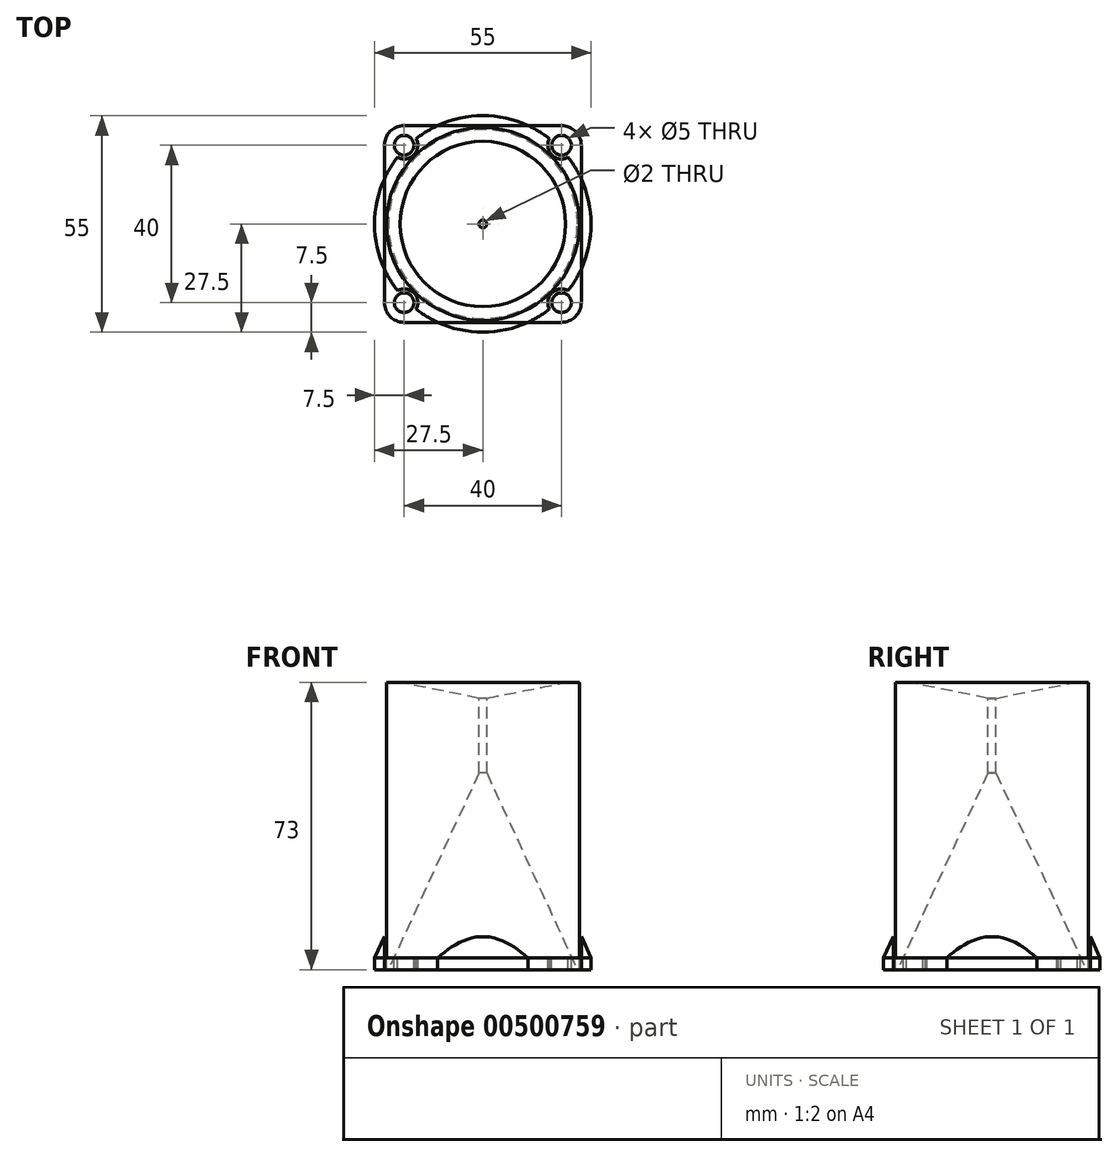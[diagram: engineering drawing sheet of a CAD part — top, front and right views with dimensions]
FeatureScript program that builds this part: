
annotation { "Feature Type Name" : "Feature", "Feature Type Description" : "" }
export const myFeature = defineFeature(function(context is Context, id is Id, definition is map)
    precondition{}
    {
        {
            var Q0;
            Q0=qCreatedBy(makeId("Top.planeOp"),FACE);
            var sketch = newSketch(context, id + "F0", { "sketchPlane" : qUnion([Q0])});
            skLineSegment(sketch, "E0.bottom", {"start": v(-25, 25) * mm, "end": v(25, 25) * mm});
            skLineSegment(sketch, "E0.top", {"start": v(-25, -25) * mm, "end": v(25, -25) * mm});
            skLineSegment(sketch, "E0.left", {"start": v(-25, 25) * mm, "end": v(-25, -25) * mm});
            skLineSegment(sketch, "E0.right", {"start": v(25, 25) * mm, "end": v(25, -25) * mm});
            skCircle(sketch, "E1", {"center": v(20, 20) * mm, "radius": 2.5 * mm});
            skCircle(sketch, "E2", {"center": v(20, -20) * mm, "radius": 2.5 * mm});
            skCircle(sketch, "E3", {"center": v(-20, -20) * mm, "radius": 2.5 * mm});
            skCircle(sketch, "E4", {"center": v(-20, 20) * mm, "radius": 2.5 * mm});
            skCircle(sketch, "E5", {"center": v(0, 0) * mm, "radius": 24.5 * mm});
            skCircle(sketch, "E6", {"center": v(-20, 20) * mm, "radius": 3.5 * mm});
            skCircle(sketch, "E7", {"center": v(20, 20) * mm, "radius": 3.5 * mm});
            skCircle(sketch, "E8", {"center": v(20, -20) * mm, "radius": 3.5 * mm});
            skCircle(sketch, "E9", {"center": v(-20, -20) * mm, "radius": 3.5 * mm});
            skCircle(sketch, "E10", {"center": v(0, 0) * mm, "radius": 1 * mm});
            skCircle(sketch, "E11", {"center": v(0, 0) * mm, "radius": 27.5 * mm});
            skSolve(sketch);
        }
        {
            var Q0;
            Q0=makeQuery(id+"F0.imprint","IMPRINT",FACE,{"disambiguationData":[TD([[makeQuery(id+"F0.imprint","IMPRINT",EDGE,{"derivedFrom":sQuery(id+"F0.wireOp",EDGE,"E0.bottom")}),-1.0]])]});
            var Q1;
            Q1=makeQuery(id+"F0.imprint","IMPRINT",FACE,{"disambiguationData":[TD([[makeQuery(id+"F0.imprint","IMPRINT",EDGE,{"derivedFrom":sQuery(id+"F0.wireOp",EDGE,"E1")}),-1.0]])]});
            var Q2;
            Q2=makeQuery(id+"F0.imprint","IMPRINT",FACE,{"disambiguationData":[TD([[makeQuery(id+"F0.imprint","IMPRINT",EDGE,{"derivedFrom":sQuery(id+"F0.wireOp",EDGE,"E2")}),-1.0]])]});
            var Q3;
            Q3=makeQuery(id+"F0.imprint","IMPRINT",FACE,{"disambiguationData":[TD([[makeQuery(id+"F0.imprint","IMPRINT",EDGE,{"derivedFrom":sQuery(id+"F0.wireOp",EDGE,"E3")}),-1.0]])]});
            var Q4;
            Q4=makeQuery(id+"F0.imprint","IMPRINT",FACE,{"disambiguationData":[TD([[makeQuery(id+"F0.imprint","IMPRINT",EDGE,{"derivedFrom":sQuery(id+"F0.wireOp",EDGE,"E4")}),-1.0]])]});
            var Q5;
            Q5=makeQuery(id+"F0.imprint","IMPRINT",FACE,{"disambiguationData":[TD([[makeQuery(id+"F0.imprint","IMPRINT",EDGE,{"derivedFrom":sQuery(id+"F0.wireOp",EDGE,"E5")}),1.0]])]});
            var Q6;
            Q6=makeQuery(id+"F0.imprint","IMPRINT",FACE,{"disambiguationData":[TD([[makeQuery(id+"F0.imprint","IMPRINT",EDGE,{"derivedFrom":sQuery(id+"F0.wireOp",EDGE,"WA1lCMuK-sLq4-XsFw-FNTR-WKbZTbo29WLb")}),1.0]])]});
            var Q7;
            Q7=makeQuery(id+"F0.imprint","IMPRINT",FACE,{"disambiguationData":[TD([[makeQuery(id+"F0.imprint","IMPRINT",EDGE,{"derivedFrom":sQuery(id+"F0.wireOp",EDGE,"E5")}),-1.0]])]});
            var Q8;
            {var subQ0=sQuery(id+"F0.wireOp",EDGE,"E11");var subQ1=sQuery(id+"F0.wireOp",EDGE,"E0.bottom");var subQ2=makeQuery(id+"F0.imprint","INTERSECT",VERTEX,{"disambiguationData":[OD(0.0)],"derivedFrom":[subQ1,subQ0]});Q8=makeQuery(id+"F0.imprint","IMPRINT",FACE,{"disambiguationData":[TD([[makeQuery(id+"F0.imprint","IMPRINT",EDGE,{"disambiguationData":[TD([[subQ2,-1.0]])],"derivedFrom":subQ1}),1.0]])]});}
            var Q9;
            {var subQ0=sQuery(id+"F0.wireOp",EDGE,"E11");var subQ1=sQuery(id+"F0.wireOp",EDGE,"E0.right");var subQ2=makeQuery(id+"F0.imprint","INTERSECT",VERTEX,{"disambiguationData":[OD(0.0)],"derivedFrom":[subQ1,subQ0]});Q9=makeQuery(id+"F0.imprint","IMPRINT",FACE,{"disambiguationData":[TD([[makeQuery(id+"F0.imprint","IMPRINT",EDGE,{"disambiguationData":[TD([[subQ2,-1.0]])],"derivedFrom":subQ1}),1.0]])]});}
            var Q10;
            {var subQ0=sQuery(id+"F0.wireOp",EDGE,"E11");var subQ1=sQuery(id+"F0.wireOp",EDGE,"E0.left");var subQ2=makeQuery(id+"F0.imprint","INTERSECT",VERTEX,{"disambiguationData":[OD(0.0)],"derivedFrom":[subQ1,subQ0]});Q10=makeQuery(id+"F0.imprint","IMPRINT",FACE,{"disambiguationData":[TD([[makeQuery(id+"F0.imprint","IMPRINT",EDGE,{"disambiguationData":[TD([[subQ2,-1.0]])],"derivedFrom":subQ1}),-1.0]])]});}
            var Q11;
            {var subQ0=sQuery(id+"F0.wireOp",EDGE,"E11");var subQ1=sQuery(id+"F0.wireOp",EDGE,"E0.top");var subQ2=makeQuery(id+"F0.imprint","INTERSECT",VERTEX,{"disambiguationData":[OD(0.0)],"derivedFrom":[subQ1,subQ0]});Q11=makeQuery(id+"F0.imprint","IMPRINT",FACE,{"disambiguationData":[TD([[makeQuery(id+"F0.imprint","IMPRINT",EDGE,{"disambiguationData":[TD([[subQ2,-1.0]])],"derivedFrom":subQ1}),-1.0]])]});}
            var Q12;
            {var subQ1=sQuery(id+"F0.wireOp",EDGE,"E0.top");var subQ6=sQuery(id+"F0.wireOp",EDGE,"E0.right");var subQ7=makeQuery(id+"F0.imprint","INTERSECT",VERTEX,{"derivedFrom":[subQ1,subQ6]});Q12=makeQuery(id+"F0.imprint","IMPRINT",FACE,{"disambiguationData":[TD([[makeQuery(id+"F0.imprint","IMPRINT",EDGE,{"disambiguationData":[TD([[subQ7,1.0]])],"derivedFrom":subQ1}),1.0]])]});}
            var Q13;
            {var subQ1=sQuery(id+"F0.wireOp",EDGE,"E0.left");var subQ6=sQuery(id+"F0.wireOp",EDGE,"E0.top");var subQ7=makeQuery(id+"F0.imprint","INTERSECT",VERTEX,{"derivedFrom":[subQ6,subQ1]});Q13=makeQuery(id+"F0.imprint","IMPRINT",FACE,{"disambiguationData":[TD([[makeQuery(id+"F0.imprint","IMPRINT",EDGE,{"disambiguationData":[TD([[subQ7,-1.0]])],"derivedFrom":subQ6}),1.0]])]});}
            extrude(context, id + "F1", {"entities" : qUnion([Q0, Q1, Q2, Q3, Q4, Q5, Q6, Q7, Q8, Q9, Q10, Q11, Q12, Q13]), "oppositeDirection" : true, "depth" : 3 * mm, "offsetDistance" : 25 * mm});
        }
        {
            var Q0;
            Q0=makeQuery(id+"F1.opExtrude","SWEPT_EDGE",EDGE,{"disambiguationData":[OSD([sQuery(id+"F0.wireOp",EDGE,"E0.bottom"),sQuery(id+"F0.wireOp",EDGE,"E0.left")])]});
            var Q1;
            Q1=makeQuery(id+"F1.opExtrude","SWEPT_EDGE",EDGE,{"disambiguationData":[OSD([sQuery(id+"F0.wireOp",EDGE,"E0.top"),sQuery(id+"F0.wireOp",EDGE,"E0.left")])]});
            var Q2;
            Q2=makeQuery(id+"F1.opExtrude","SWEPT_EDGE",EDGE,{"disambiguationData":[OSD([sQuery(id+"F0.wireOp",EDGE,"E0.top"),sQuery(id+"F0.wireOp",EDGE,"E0.right")])]});
            var Q3;
            Q3=makeQuery(id+"F1.opExtrude","SWEPT_EDGE",EDGE,{"disambiguationData":[OSD([sQuery(id+"F0.wireOp",EDGE,"E0.bottom"),sQuery(id+"F0.wireOp",EDGE,"E0.right")])]});
            fillet(context, id + "F2", {"entities" : qUnion([Q0, Q1, Q2, Q3]), "radius" : 5 * mm, "tangentPropagation" : true, "allowEdgeOverflow" : false});
        }
        {
            var Q0;
            Q0=makeQuery(id+"F0.imprint","IMPRINT",FACE,{"disambiguationData":[TD([[makeQuery(id+"F0.imprint","IMPRINT",EDGE,{"derivedFrom":sQuery(id+"F0.wireOp",EDGE,"E5")}),1.0]])]});
            var Q1;
            Q1=makeQuery(id+"F0.imprint","IMPRINT",FACE,{"disambiguationData":[TD([[makeQuery(id+"F0.imprint","IMPRINT",EDGE,{"derivedFrom":sQuery(id+"F0.wireOp",EDGE,"E5")}),-1.0]])]});
            var Q2;
            {var subQ0=sQuery(id+"F0.wireOp",EDGE,"E11");var subQ1=sQuery(id+"F0.wireOp",EDGE,"E1");var subQ2=makeQuery(id+"F0.imprint","INTERSECT",VERTEX,{"disambiguationData":[OD(0.0)],"derivedFrom":[subQ1,subQ0]});Q2=makeQuery(id+"F0.imprint","IMPRINT",FACE,{"disambiguationData":[TD([[makeQuery(id+"F0.imprint","IMPRINT",EDGE,{"disambiguationData":[TD([[subQ2,1.0]])],"derivedFrom":subQ1}),1.0]])]});}
            var Q3;
            {var subQ0=sQuery(id+"F0.wireOp",EDGE,"E11");var subQ1=sQuery(id+"F0.wireOp",EDGE,"E4");var subQ2=makeQuery(id+"F0.imprint","INTERSECT",VERTEX,{"disambiguationData":[OD(0.0)],"derivedFrom":[subQ1,subQ0]});Q3=makeQuery(id+"F0.imprint","IMPRINT",FACE,{"disambiguationData":[TD([[makeQuery(id+"F0.imprint","IMPRINT",EDGE,{"disambiguationData":[TD([[subQ2,1.0]])],"derivedFrom":subQ1}),-1.0]])]});}
            var Q4;
            {var subQ0=sQuery(id+"F0.wireOp",EDGE,"E11");var subQ1=sQuery(id+"F0.wireOp",EDGE,"E4");var subQ2=makeQuery(id+"F0.imprint","INTERSECT",VERTEX,{"disambiguationData":[OD(0.0)],"derivedFrom":[subQ1,subQ0]});Q4=makeQuery(id+"F0.imprint","IMPRINT",FACE,{"disambiguationData":[TD([[makeQuery(id+"F0.imprint","IMPRINT",EDGE,{"disambiguationData":[TD([[subQ2,1.0]])],"derivedFrom":subQ1}),1.0]])]});}
            var Q5;
            {var subQ0=sQuery(id+"F0.wireOp",EDGE,"E11");var subQ1=sQuery(id+"F0.wireOp",EDGE,"E0.left");var subQ2=makeQuery(id+"F0.imprint","INTERSECT",VERTEX,{"disambiguationData":[OD(0.0)],"derivedFrom":[subQ1,subQ0]});Q5=makeQuery(id+"F0.imprint","IMPRINT",FACE,{"disambiguationData":[TD([[makeQuery(id+"F0.imprint","IMPRINT",EDGE,{"disambiguationData":[TD([[subQ2,-1.0]])],"derivedFrom":subQ1}),-1.0]])]});}
            var Q6;
            {var subQ0=sQuery(id+"F0.wireOp",EDGE,"E11");var subQ1=sQuery(id+"F0.wireOp",EDGE,"E0.bottom");var subQ2=makeQuery(id+"F0.imprint","INTERSECT",VERTEX,{"disambiguationData":[OD(0.0)],"derivedFrom":[subQ1,subQ0]});Q6=makeQuery(id+"F0.imprint","IMPRINT",FACE,{"disambiguationData":[TD([[makeQuery(id+"F0.imprint","IMPRINT",EDGE,{"disambiguationData":[TD([[subQ2,-1.0]])],"derivedFrom":subQ1}),1.0]])]});}
            var Q7;
            {var subQ0=sQuery(id+"F0.wireOp",EDGE,"E11");var subQ1=sQuery(id+"F0.wireOp",EDGE,"E1");var subQ2=makeQuery(id+"F0.imprint","INTERSECT",VERTEX,{"disambiguationData":[OD(0.0)],"derivedFrom":[subQ1,subQ0]});Q7=makeQuery(id+"F0.imprint","IMPRINT",FACE,{"disambiguationData":[TD([[makeQuery(id+"F0.imprint","IMPRINT",EDGE,{"disambiguationData":[TD([[subQ2,1.0]])],"derivedFrom":subQ1}),-1.0]])]});}
            var Q8;
            {var subQ0=sQuery(id+"F0.wireOp",EDGE,"E11");var subQ1=sQuery(id+"F0.wireOp",EDGE,"E0.right");var subQ2=makeQuery(id+"F0.imprint","INTERSECT",VERTEX,{"disambiguationData":[OD(0.0)],"derivedFrom":[subQ1,subQ0]});Q8=makeQuery(id+"F0.imprint","IMPRINT",FACE,{"disambiguationData":[TD([[makeQuery(id+"F0.imprint","IMPRINT",EDGE,{"disambiguationData":[TD([[subQ2,-1.0]])],"derivedFrom":subQ1}),1.0]])]});}
            var Q9;
            {var subQ0=sQuery(id+"F0.wireOp",EDGE,"E11");var subQ1=sQuery(id+"F0.wireOp",EDGE,"E2");var subQ2=makeQuery(id+"F0.imprint","INTERSECT",VERTEX,{"disambiguationData":[OD(0.0)],"derivedFrom":[subQ1,subQ0]});Q9=makeQuery(id+"F0.imprint","IMPRINT",FACE,{"disambiguationData":[TD([[makeQuery(id+"F0.imprint","IMPRINT",EDGE,{"disambiguationData":[TD([[subQ2,1.0]])],"derivedFrom":subQ1}),-1.0]])]});}
            var Q10;
            {var subQ0=sQuery(id+"F0.wireOp",EDGE,"E11");var subQ1=sQuery(id+"F0.wireOp",EDGE,"E2");var subQ2=makeQuery(id+"F0.imprint","INTERSECT",VERTEX,{"disambiguationData":[OD(0.0)],"derivedFrom":[subQ1,subQ0]});Q10=makeQuery(id+"F0.imprint","IMPRINT",FACE,{"disambiguationData":[TD([[makeQuery(id+"F0.imprint","IMPRINT",EDGE,{"disambiguationData":[TD([[subQ2,1.0]])],"derivedFrom":subQ1}),1.0]])]});}
            var Q11;
            {var subQ0=sQuery(id+"F0.wireOp",EDGE,"E11");var subQ1=sQuery(id+"F0.wireOp",EDGE,"E0.top");var subQ2=makeQuery(id+"F0.imprint","INTERSECT",VERTEX,{"disambiguationData":[OD(0.0)],"derivedFrom":[subQ1,subQ0]});Q11=makeQuery(id+"F0.imprint","IMPRINT",FACE,{"disambiguationData":[TD([[makeQuery(id+"F0.imprint","IMPRINT",EDGE,{"disambiguationData":[TD([[subQ2,-1.0]])],"derivedFrom":subQ1}),-1.0]])]});}
            var Q12;
            {var subQ0=sQuery(id+"F0.wireOp",EDGE,"E11");var subQ1=sQuery(id+"F0.wireOp",EDGE,"E3");var subQ2=makeQuery(id+"F0.imprint","INTERSECT",VERTEX,{"disambiguationData":[OD(0.0)],"derivedFrom":[subQ1,subQ0]});Q12=makeQuery(id+"F0.imprint","IMPRINT",FACE,{"disambiguationData":[TD([[makeQuery(id+"F0.imprint","IMPRINT",EDGE,{"disambiguationData":[TD([[subQ2,1.0]])],"derivedFrom":subQ1}),1.0]])]});}
            var Q13;
            {var subQ0=sQuery(id+"F0.wireOp",EDGE,"E11");var subQ1=sQuery(id+"F0.wireOp",EDGE,"E3");var subQ2=makeQuery(id+"F0.imprint","INTERSECT",VERTEX,{"disambiguationData":[OD(0.0)],"derivedFrom":[subQ1,subQ0]});Q13=makeQuery(id+"F0.imprint","IMPRINT",FACE,{"disambiguationData":[TD([[makeQuery(id+"F0.imprint","IMPRINT",EDGE,{"disambiguationData":[TD([[subQ2,1.0]])],"derivedFrom":subQ1}),-1.0]])]});}
            extrude(context, id + "F3", {"entities" : qUnion([Q0, Q1, Q2, Q3, Q4, Q5, Q6, Q7, Q8, Q9, Q10, Q11, Q12, Q13]), "operationType" : NewBodyOperationType.ADD, "depth" : 50 * mm, "offsetDistance" : 25 * mm});
        }
        {
            var Q0;
            Q0=makeQuery(id+"F3.opExtrude","CAP_EDGE",EDGE,{"disambiguationData":[OSD([sQuery(id+"F0.wireOp",EDGE,"E11")])],"isStart":false});
            chamfer(context, id + "F4", {"entities" : qUnion([Q0]), "chamferType" : ChamferType.TWO_OFFSETS, "width1" : 23 * mm, "oppositeDirection" : false, "width2" : 50 * mm, "tangentPropagation" : true});
        }
        {
            var Q0;
            {var subQ0=sQuery(id+"F0.wireOp",EDGE,"E11");var subQ1=sQuery(id+"F0.wireOp",EDGE,"E1");var subQ2=makeQuery(id+"F0.imprint","INTERSECT",VERTEX,{"disambiguationData":[OD(0.0)],"derivedFrom":[subQ1,subQ0]});Q0=makeQuery(id+"F0.imprint","IMPRINT",FACE,{"disambiguationData":[TD([[makeQuery(id+"F0.imprint","IMPRINT",EDGE,{"disambiguationData":[TD([[subQ2,1.0]])],"derivedFrom":subQ1}),1.0]])]});}
            var Q1;
            {var subQ0=sQuery(id+"F0.wireOp",EDGE,"E11");var subQ1=sQuery(id+"F0.wireOp",EDGE,"E1");var subQ2=makeQuery(id+"F0.imprint","INTERSECT",VERTEX,{"disambiguationData":[OD(0.0)],"derivedFrom":[subQ1,subQ0]});Q1=makeQuery(id+"F0.imprint","IMPRINT",FACE,{"disambiguationData":[TD([[makeQuery(id+"F0.imprint","IMPRINT",EDGE,{"disambiguationData":[TD([[subQ2,1.0]])],"derivedFrom":subQ1}),-1.0]])]});}
            var Q2;
            {var subQ0=sQuery(id+"F0.wireOp",EDGE,"E11");var subQ1=sQuery(id+"F0.wireOp",EDGE,"E1");var subQ2=makeQuery(id+"F0.imprint","INTERSECT",VERTEX,{"disambiguationData":[OD(0.0)],"derivedFrom":[subQ1,subQ0]});Q2=makeQuery(id+"F0.imprint","IMPRINT",FACE,{"disambiguationData":[TD([[makeQuery(id+"F0.imprint","IMPRINT",EDGE,{"disambiguationData":[TD([[subQ2,-1.0]])],"derivedFrom":subQ1}),-1.0]])]});}
            var Q3;
            {var subQ0=sQuery(id+"F0.wireOp",EDGE,"E11");var subQ1=sQuery(id+"F0.wireOp",EDGE,"E4");var subQ2=makeQuery(id+"F0.imprint","INTERSECT",VERTEX,{"disambiguationData":[OD(0.0)],"derivedFrom":[subQ1,subQ0]});Q3=makeQuery(id+"F0.imprint","IMPRINT",FACE,{"disambiguationData":[TD([[makeQuery(id+"F0.imprint","IMPRINT",EDGE,{"disambiguationData":[TD([[subQ2,1.0]])],"derivedFrom":subQ1}),1.0]])]});}
            var Q4;
            {var subQ0=sQuery(id+"F0.wireOp",EDGE,"E11");var subQ1=sQuery(id+"F0.wireOp",EDGE,"E4");var subQ2=makeQuery(id+"F0.imprint","INTERSECT",VERTEX,{"disambiguationData":[OD(0.0)],"derivedFrom":[subQ1,subQ0]});Q4=makeQuery(id+"F0.imprint","IMPRINT",FACE,{"disambiguationData":[TD([[makeQuery(id+"F0.imprint","IMPRINT",EDGE,{"disambiguationData":[TD([[subQ2,1.0]])],"derivedFrom":subQ1}),-1.0]])]});}
            var Q5;
            {var subQ0=sQuery(id+"F0.wireOp",EDGE,"E11");var subQ1=sQuery(id+"F0.wireOp",EDGE,"E4");var subQ2=makeQuery(id+"F0.imprint","INTERSECT",VERTEX,{"disambiguationData":[OD(0.0)],"derivedFrom":[subQ1,subQ0]});Q5=makeQuery(id+"F0.imprint","IMPRINT",FACE,{"disambiguationData":[TD([[makeQuery(id+"F0.imprint","IMPRINT",EDGE,{"disambiguationData":[TD([[subQ2,-1.0]])],"derivedFrom":subQ1}),-1.0]])]});}
            var Q6;
            {var subQ0=sQuery(id+"F0.wireOp",EDGE,"E11");var subQ1=sQuery(id+"F0.wireOp",EDGE,"E4");var subQ2=makeQuery(id+"F0.imprint","INTERSECT",VERTEX,{"disambiguationData":[OD(0.0)],"derivedFrom":[subQ1,subQ0]});Q6=makeQuery(id+"F0.imprint","IMPRINT",FACE,{"disambiguationData":[TD([[makeQuery(id+"F0.imprint","IMPRINT",EDGE,{"disambiguationData":[TD([[subQ2,-1.0]])],"derivedFrom":subQ1}),1.0]])]});}
            var Q7;
            {var subQ0=sQuery(id+"F0.wireOp",EDGE,"E11");var subQ1=sQuery(id+"F0.wireOp",EDGE,"E1");var subQ2=makeQuery(id+"F0.imprint","INTERSECT",VERTEX,{"disambiguationData":[OD(0.0)],"derivedFrom":[subQ1,subQ0]});Q7=makeQuery(id+"F0.imprint","IMPRINT",FACE,{"disambiguationData":[TD([[makeQuery(id+"F0.imprint","IMPRINT",EDGE,{"disambiguationData":[TD([[subQ2,-1.0]])],"derivedFrom":subQ1}),1.0]])]});}
            var Q8;
            {var subQ0=sQuery(id+"F0.wireOp",EDGE,"E11");var subQ1=sQuery(id+"F0.wireOp",EDGE,"E2");var subQ2=makeQuery(id+"F0.imprint","INTERSECT",VERTEX,{"disambiguationData":[OD(0.0)],"derivedFrom":[subQ1,subQ0]});Q8=makeQuery(id+"F0.imprint","IMPRINT",FACE,{"disambiguationData":[TD([[makeQuery(id+"F0.imprint","IMPRINT",EDGE,{"disambiguationData":[TD([[subQ2,1.0]])],"derivedFrom":subQ1}),1.0]])]});}
            var Q9;
            {var subQ0=sQuery(id+"F0.wireOp",EDGE,"E11");var subQ1=sQuery(id+"F0.wireOp",EDGE,"E2");var subQ2=makeQuery(id+"F0.imprint","INTERSECT",VERTEX,{"disambiguationData":[OD(0.0)],"derivedFrom":[subQ1,subQ0]});Q9=makeQuery(id+"F0.imprint","IMPRINT",FACE,{"disambiguationData":[TD([[makeQuery(id+"F0.imprint","IMPRINT",EDGE,{"disambiguationData":[TD([[subQ2,-1.0]])],"derivedFrom":subQ1}),1.0]])]});}
            var Q10;
            {var subQ0=sQuery(id+"F0.wireOp",EDGE,"E11");var subQ1=sQuery(id+"F0.wireOp",EDGE,"E2");var subQ2=makeQuery(id+"F0.imprint","INTERSECT",VERTEX,{"disambiguationData":[OD(0.0)],"derivedFrom":[subQ1,subQ0]});Q10=makeQuery(id+"F0.imprint","IMPRINT",FACE,{"disambiguationData":[TD([[makeQuery(id+"F0.imprint","IMPRINT",EDGE,{"disambiguationData":[TD([[subQ2,-1.0]])],"derivedFrom":subQ1}),-1.0]])]});}
            var Q11;
            {var subQ0=sQuery(id+"F0.wireOp",EDGE,"E11");var subQ1=sQuery(id+"F0.wireOp",EDGE,"E2");var subQ2=makeQuery(id+"F0.imprint","INTERSECT",VERTEX,{"disambiguationData":[OD(0.0)],"derivedFrom":[subQ1,subQ0]});Q11=makeQuery(id+"F0.imprint","IMPRINT",FACE,{"disambiguationData":[TD([[makeQuery(id+"F0.imprint","IMPRINT",EDGE,{"disambiguationData":[TD([[subQ2,1.0]])],"derivedFrom":subQ1}),-1.0]])]});}
            var Q12;
            {var subQ0=sQuery(id+"F0.wireOp",EDGE,"E11");var subQ1=sQuery(id+"F0.wireOp",EDGE,"E3");var subQ2=makeQuery(id+"F0.imprint","INTERSECT",VERTEX,{"disambiguationData":[OD(0.0)],"derivedFrom":[subQ1,subQ0]});Q12=makeQuery(id+"F0.imprint","IMPRINT",FACE,{"disambiguationData":[TD([[makeQuery(id+"F0.imprint","IMPRINT",EDGE,{"disambiguationData":[TD([[subQ2,-1.0]])],"derivedFrom":subQ1}),1.0]])]});}
            var Q13;
            {var subQ0=sQuery(id+"F0.wireOp",EDGE,"E11");var subQ1=sQuery(id+"F0.wireOp",EDGE,"E3");var subQ2=makeQuery(id+"F0.imprint","INTERSECT",VERTEX,{"disambiguationData":[OD(0.0)],"derivedFrom":[subQ1,subQ0]});Q13=makeQuery(id+"F0.imprint","IMPRINT",FACE,{"disambiguationData":[TD([[makeQuery(id+"F0.imprint","IMPRINT",EDGE,{"disambiguationData":[TD([[subQ2,1.0]])],"derivedFrom":subQ1}),1.0]])]});}
            var Q14;
            {var subQ0=sQuery(id+"F0.wireOp",EDGE,"E11");var subQ1=sQuery(id+"F0.wireOp",EDGE,"E3");var subQ2=makeQuery(id+"F0.imprint","INTERSECT",VERTEX,{"disambiguationData":[OD(0.0)],"derivedFrom":[subQ1,subQ0]});Q14=makeQuery(id+"F0.imprint","IMPRINT",FACE,{"disambiguationData":[TD([[makeQuery(id+"F0.imprint","IMPRINT",EDGE,{"disambiguationData":[TD([[subQ2,1.0]])],"derivedFrom":subQ1}),-1.0]])]});}
            var Q15;
            {var subQ0=sQuery(id+"F0.wireOp",EDGE,"E11");var subQ1=sQuery(id+"F0.wireOp",EDGE,"E3");var subQ2=makeQuery(id+"F0.imprint","INTERSECT",VERTEX,{"disambiguationData":[OD(0.0)],"derivedFrom":[subQ1,subQ0]});Q15=makeQuery(id+"F0.imprint","IMPRINT",FACE,{"disambiguationData":[TD([[makeQuery(id+"F0.imprint","IMPRINT",EDGE,{"disambiguationData":[TD([[subQ2,-1.0]])],"derivedFrom":subQ1}),-1.0]])]});}
            extrude(context, id + "F5", {"entities" : qUnion([Q0, Q1, Q2, Q3, Q4, Q5, Q6, Q7, Q8, Q9, Q10, Q11, Q12, Q13, Q14, Q15]), "operationType" : NewBodyOperationType.REMOVE, "depth" : 25 * mm, "offsetDistance" : 25 * mm});
        }
        {
            var Q0;
            Q0=makeQuery(id+"F1.opExtrude","CAP_EDGE",EDGE,{"disambiguationData":[OSD([sQuery(id+"F0.wireOp",EDGE,"E10")])],"isStart":false});
            chamfer(context, id + "F6", {"entities" : qUnion([Q0]), "chamferType" : ChamferType.TWO_OFFSETS, "width1" : 23 * mm, "oppositeDirection" : false, "width2" : 50 * mm, "tangentPropagation" : true});
        }
        {
            var Q0;
            Q0=makeQuery(id+"F3.opExtrude","CAP_FACE",FACE,{"disambiguationData":[OSD([sQuery(id+"F0.wireOp",EDGE,"E10"),sQuery(id+"F0.wireOp",EDGE,"E11")])],"isStart":false});
            extrude(context, id + "F7", {"entities" : qUnion([Q0]), "operationType" : NewBodyOperationType.ADD, "depth" : 20 * mm, "offsetDistance" : 25 * mm});
        }
        {
            var Q0;
            Q0=makeQuery(id+"F7.opExtrude","CAP_EDGE",EDGE,{"disambiguationData":[OSD([sQuery(id+"F0.wireOp",EDGE,"E10"),sQuery(id+"F0.wireOp",EDGE,"E11")])],"isStart":false});
            chamfer(context, id + "F8", {"entities" : qUnion([Q0]), "chamferType" : ChamferType.TWO_OFFSETS, "width1" : 4 * mm, "oppositeDirection" : false, "width2" : 20 * mm, "tangentPropagation" : true});
        }
    });
